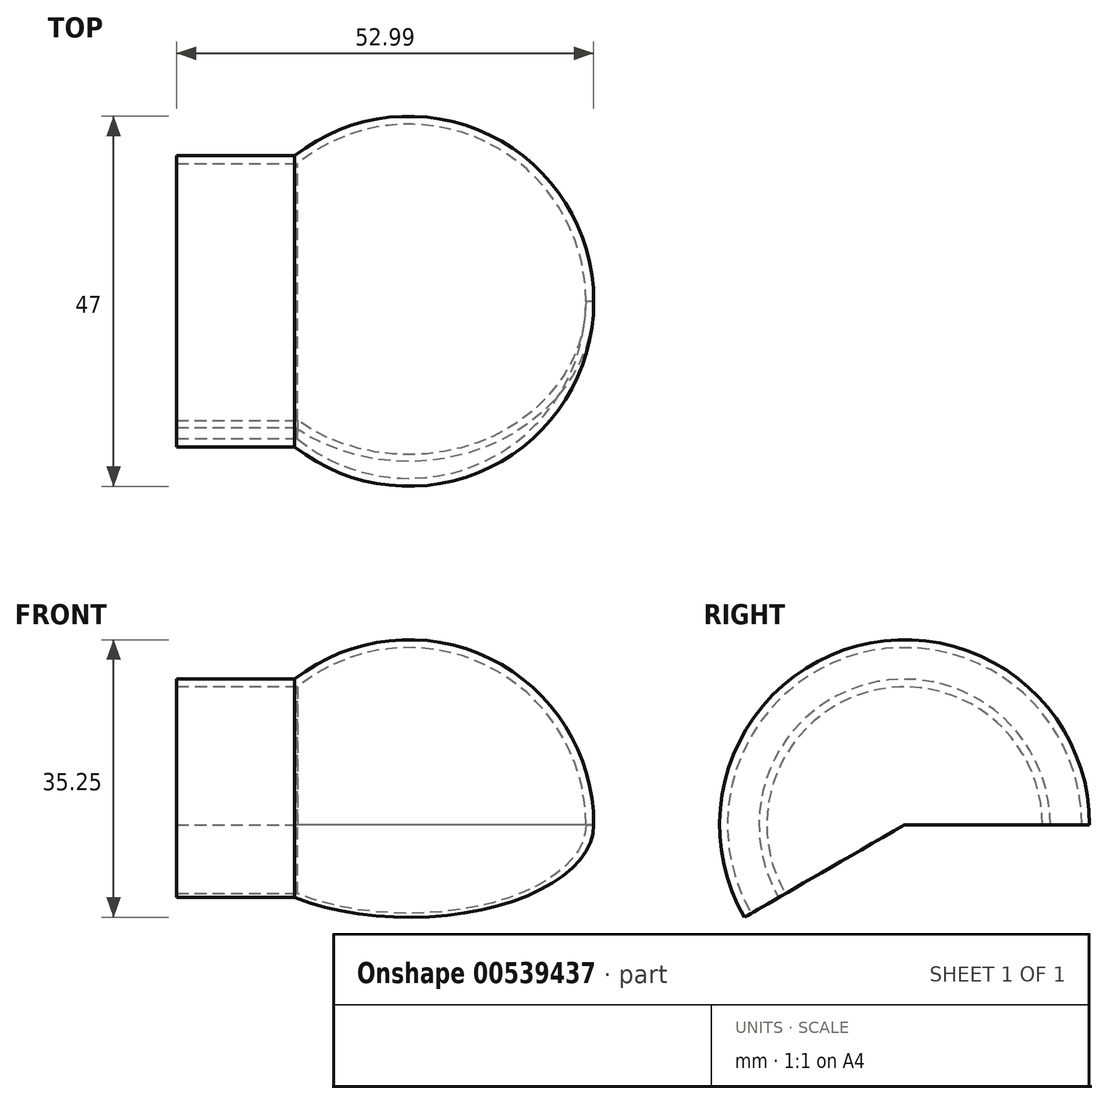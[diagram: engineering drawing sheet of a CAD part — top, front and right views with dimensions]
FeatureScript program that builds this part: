
annotation { "Feature Type Name" : "Feature", "Feature Type Description" : "" }
export const myFeature = defineFeature(function(context is Context, id is Id, definition is map)
    precondition{}
    {
        {
            var Q0;
            Q0=qCreatedBy(makeId("Top.planeOp"),FACE);
            var sketch = newSketch(context, id + "F0", { "sketchPlane" : qUnion([Q0])});
            skCircle(sketch, "E0", {"center": v(-36.94, 36.35) * mm, "radius": 23.5 * mm});
            skLineSegment(sketch, "E1", {"start": v(-36.94, 36.35) * mm, "end": v(-66.43, 36.35) * mm});
            skLineSegment(sketch, "E2", {"start": v(-66.43, 36.35) * mm, "end": v(-66.43, 54.85) * mm});
            skLineSegment(sketch, "E3", {"start": v(-66.43, 54.85) * mm, "end": v(-51.43, 54.85) * mm});
            skLineSegment(sketch, "E4", {"start": v(-51.43, 54.85) * mm, "end": v(-51.43, 17.85) * mm});
            skLineSegment(sketch, "E5", {"start": v(-51.43, 17.85) * mm, "end": v(-66.43, 17.85) * mm});
            skLineSegment(sketch, "E6", {"start": v(-66.43, 17.85) * mm, "end": v(-66.43, 36.35) * mm});
            skLineSegment(sketch, "E7", {"start": v(-83.88, 36.35) * mm, "end": v(16.2, 36.35) * mm});
            skLineSegment(sketch, "E8", {"start": v(-66.43, 53.85) * mm, "end": v(-50.35, 53.85) * mm});
            skCircle(sketch, "E9", {"center": v(-36.94, 36.35) * mm, "radius": 22.5 * mm});
            skSolve(sketch);
        }
        {
            var Q0;
            {var subQ0=sQuery(id+"F0.wireOp",EDGE,"E3");Q0=makeQuery(id+"F0.imprint","IMPRINT",FACE,{"disambiguationData":[TD([[makeQuery(id+"F0.imprint","IMPRINT",EDGE,{"derivedFrom":subQ0}),-1.0]])]});}
            var Q1;
            {var subQ1=sQuery(id+"F0.wireOp",EDGE,"E0");var subQ3=sQuery(id+"F0.wireOp",EDGE,"E7");var subQ4=makeQuery(id+"F0.imprint","INTERSECT",VERTEX,{"disambiguationData":[OD(0.0)],"derivedFrom":[subQ1,subQ3]});Q1=makeQuery(id+"F0.imprint","IMPRINT",FACE,{"disambiguationData":[TD([[makeQuery(id+"F0.imprint","IMPRINT",EDGE,{"disambiguationData":[TD([[subQ4,1.0]])],"derivedFrom":subQ3}),1.0]])]});}
            var Q2;
            {var subQ1=sQuery(id+"F0.wireOp",EDGE,"E0");var subQ3=sQuery(id+"F0.wireOp",EDGE,"E8");var subQ4=makeQuery(id+"F0.imprint","INTERSECT",VERTEX,{"derivedFrom":[subQ1,subQ3]});Q2=makeQuery(id+"F0.imprint","IMPRINT",FACE,{"disambiguationData":[TD([[makeQuery(id+"F0.imprint","IMPRINT",EDGE,{"disambiguationData":[TD([[subQ4,-1.0]])],"derivedFrom":subQ3}),1.0]])]});}
            var Q3;
            Q3=sQuery(id+"F0.wireOp",EDGE,"E5");
            var Q4;
            Q4=sQuery(id+"F0.wireOp",EDGE,"E0");
            var Q5;
            Q5=sQuery(id+"F0.wireOp",EDGE,"E7");
            revolve(context, id + "F1", {"entities" : qUnion([Q0, Q1, Q2]), "surfaceEntities" : qUnion([Q3, Q4]), "axis" : qUnion([Q5]), "revolveType" : RevolveType.ONE_DIRECTION, "angle" : 210 * degree});
        }
    });
